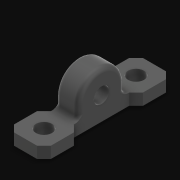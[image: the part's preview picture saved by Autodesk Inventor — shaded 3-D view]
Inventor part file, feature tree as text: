
AUTODESK INVENTOR PART (.ipt)
format: ipt  version: 2021 (Build 250183000, 183)  size: 220,160 bytes
history: native  units: in
note: dims shown in document units (in); Inventor stores cm internally (conversion verified against a paired STEP export)
features: extrude x3, sketch x3, fillet x1
ambient origin geometry x8: Origin, YZ Plane, XZ Plane, XY Plane, X Axis, Y Axis, Z Axis, Center Point
bodies: Solid1 (feature_tree)
feature tree (7):
  extrude  "Extrusion1"  Depth=0.173in
  extrude  "Extrusion2"  Depth=0.4in
  extrude  "Extrusion3"  Depth=0.05in
  fillet  "Fillet1"  Radius=0.4in
  sketch  "Sketch1"  dims[d2=0.173in d3=0.173in]
  sketch  "Sketch2"  dims[d4=1.0in d8=0.4in]
  sketch  "Sketch3"  dims[d9=0.4in d10=0.4in d11=0.4in d12=0.6in d13=0.2in d14=0.2in d15=0.2in d16=0.25in d17=0.075in d18=0.075in d19=0.075in d20=0.075in d21=0.075in d22=0.075in d23=0.075in d24=0.075in d25=0.075in d26=0.075in d27=0.075in d28=0.075in d29=0.075in d30=0.075in d31=0.075in d32=0.075in d33=0.075in d34=0.125in d35=0.0in d36=0.176in d37=0.176in d38=0.037in d39=0.612in d40=0.02in d41=0.027in d42=0.0in d43=0.167in d44=0.25in d45=0.3in d46=0.5in d47=0.5in d48=0.25in d49=0.25in d50=0.027in d51=0.0in d52=0.05in]
